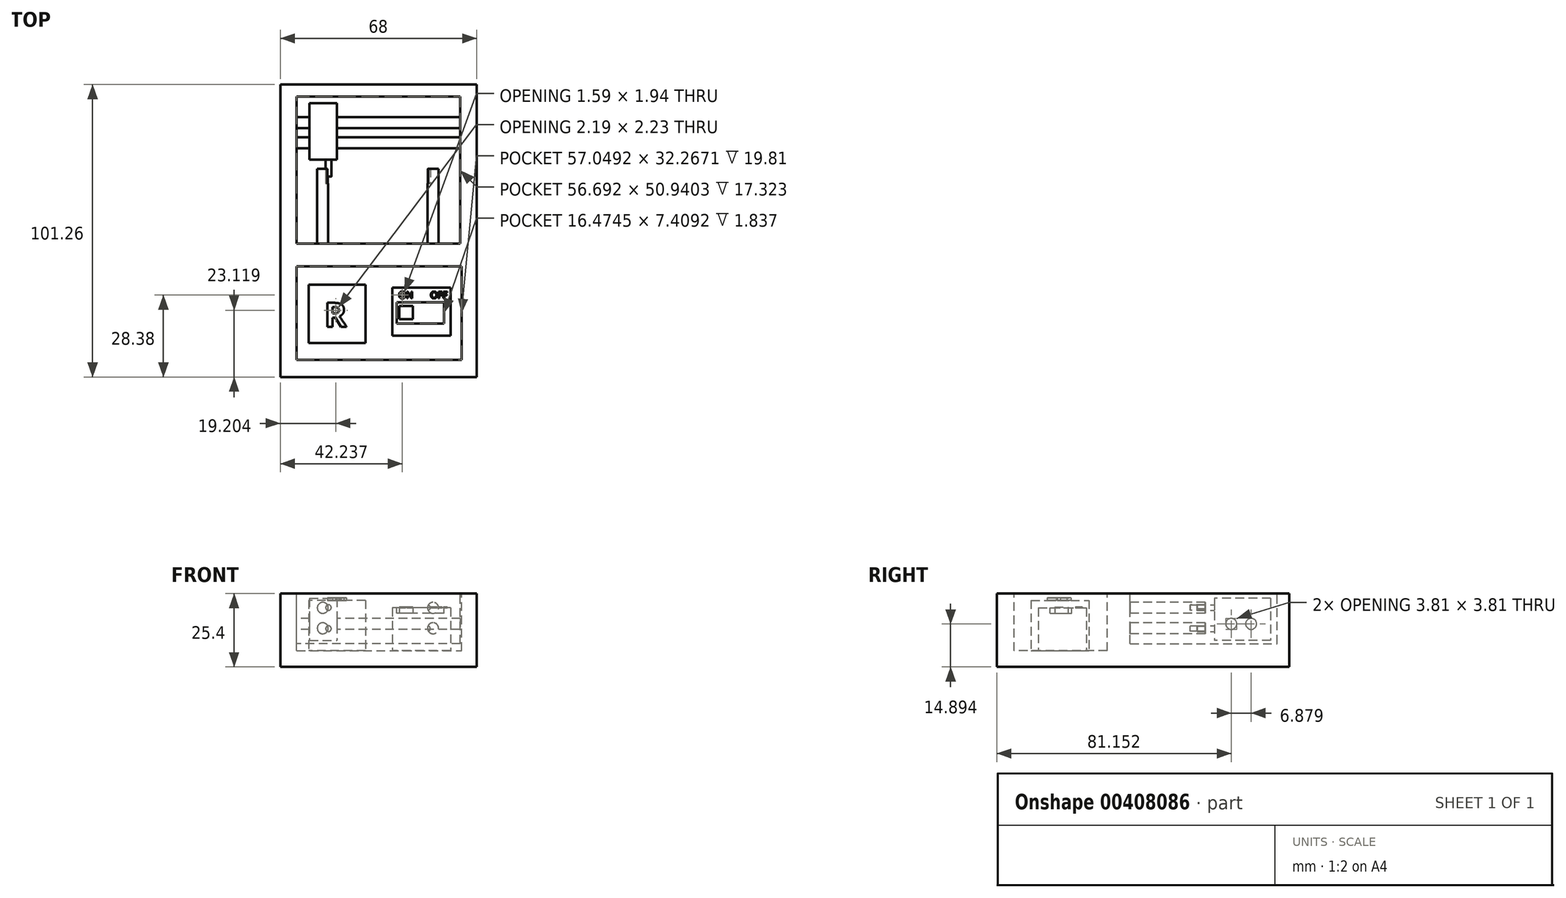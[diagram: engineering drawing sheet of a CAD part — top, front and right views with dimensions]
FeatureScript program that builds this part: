
annotation { "Feature Type Name" : "Feature", "Feature Type Description" : "" }
export const myFeature = defineFeature(function(context is Context, id is Id, definition is map)
    precondition{}
    {
        {
            var Q0;
            Q0=qCreatedBy(makeId("Top.planeOp"),FACE);
            var sketch = newSketch(context, id + "F0", { "sketchPlane" : qUnion([Q0])});
            skLineSegment(sketch, "E0.bottom", {"start": v(34, -50.63) * mm, "end": v(-34, -50.63) * mm});
            skLineSegment(sketch, "E0.top", {"start": v(34, 50.63) * mm, "end": v(-34, 50.63) * mm});
            skLineSegment(sketch, "E0.left", {"start": v(34, -50.63) * mm, "end": v(34, 50.63) * mm});
            skLineSegment(sketch, "E0.right", {"start": v(-34, -50.63) * mm, "end": v(-34, 50.63) * mm});
            skPoint(sketch, "E0.middle", {"position": v(0, 0) * mm});
            skSolve(sketch);
        }
        {
            var Q0;
            Q0 = qSketchRegion(id + "F0", true);
            extrude(context, id + "F1", {"entities" : qUnion([Q0]), "depth" : 25.4 * mm});
        }
        {
            var Q0;
            Q0=makeQuery(id+"F1.opExtrude","CAP_FACE",FACE,{"disambiguationData":[OSD([sQuery(id+"F0.wireOp",EDGE,"E0.bottom"),sQuery(id+"F0.wireOp",EDGE,"E0.top"),sQuery(id+"F0.wireOp",EDGE,"E0.left"),sQuery(id+"F0.wireOp",EDGE,"E0.right")])],"isStart":false});
            var sketch = newSketch(context, id + "F2", { "sketchPlane" : qUnion([Q0])});
            skLineSegment(sketch, "E1.bottom", {"start": v(-28.3, -12.38) * mm, "end": v(28.74, -12.38) * mm});
            skLineSegment(sketch, "E1.top", {"start": v(-28.3, -44.65) * mm, "end": v(28.74, -44.65) * mm});
            skLineSegment(sketch, "E1.left", {"start": v(-28.3, -12.38) * mm, "end": v(-28.3, -44.65) * mm});
            skLineSegment(sketch, "E1.right", {"start": v(28.74, -12.38) * mm, "end": v(28.74, -44.65) * mm});
            skSolve(sketch);
        }
        {
            var Q0;
            Q0=makeQuery(id+"F2.imprint","IMPRINT",FACE,{"disambiguationData":[TD([[makeQuery(id+"F2.imprint","IMPRINT",EDGE,{"derivedFrom":sQuery(id+"F2.wireOp",EDGE,"E1.bottom")}),-1.0]])]});
            extrude(context, id + "F3", {"entities" : qUnion([Q0]), "operationType" : NewBodyOperationType.REMOVE, "oppositeDirection" : true, "depth" : 19.8 * mm});
        }
        {
            var Q0;
            Q0=makeQuery(id+"F3.boolean.opBoolean","COPY",FACE,{"derivedFrom":makeQuery(id+"F3.opExtrude","CAP_FACE",FACE,{"disambiguationData":[OSD([sQuery(id+"F2.wireOp",EDGE,"E1.bottom"),sQuery(id+"F2.wireOp",EDGE,"E1.top"),sQuery(id+"F2.wireOp",EDGE,"E1.left"),sQuery(id+"F2.wireOp",EDGE,"E1.right")])],"isStart":false})});
            var sketch = newSketch(context, id + "F4", { "sketchPlane" : qUnion([Q0])});
            skLineSegment(sketch, "E2.bottom", {"start": v(-4.5, -38.83) * mm, "end": v(-24.11, -38.83) * mm});
            skLineSegment(sketch, "E2.top", {"start": v(-4.5, -18.71) * mm, "end": v(-24.11, -18.71) * mm});
            skLineSegment(sketch, "E2.left", {"start": v(-4.5, -38.83) * mm, "end": v(-4.5, -18.71) * mm});
            skLineSegment(sketch, "E2.right", {"start": v(-24.11, -38.83) * mm, "end": v(-24.11, -18.71) * mm});
            skPoint(sketch, "E2.middle", {"position": v(-14.3, -28.77) * mm});
            skSolve(sketch);
        }
        {
            var Q0;
            Q0 = qSketchRegion(id + "F4", true);
            extrude(context, id + "F5", {"entities" : qUnion([Q0]), "depth" : 17.46 * mm});
        }
        {
            var Q0;
            Q0=makeQuery(id+"F5.opExtrude","CAP_FACE",FACE,{"disambiguationData":[OSD([sQuery(id+"F4.wireOp",EDGE,"E2.bottom"),sQuery(id+"F4.wireOp",EDGE,"E2.top"),sQuery(id+"F4.wireOp",EDGE,"E2.left"),sQuery(id+"F4.wireOp",EDGE,"E2.right")])],"isStart":false});
            var sketch = newSketch(context, id + "F6", { "sketchPlane" : qUnion([Q0])});
            skText(sketch, "E3", { "text": "R", "fontName": "OpenSans-Bold.ttf"});
            const initialGuessF6  = {"E3": [-0.01868, -0.03322, 1, 0, 0.00833]};
            skSetInitialGuess(sketch, initialGuessF6);
            skSolve(sketch);
        }
        {
            var Q0;
            Q0 = qSketchRegion(id + "F6", true);
            extrude(context, id + "F7", {"entities" : qUnion([Q0]), "depth" : 0.9 * mm});
        }
        {
            var Q0;
            Q0=makeQuery(id+"F3.boolean.opBoolean","COPY",FACE,{"derivedFrom":makeQuery(id+"F3.opExtrude","CAP_FACE",FACE,{"disambiguationData":[OSD([sQuery(id+"F2.wireOp",EDGE,"E1.bottom"),sQuery(id+"F2.wireOp",EDGE,"E1.top"),sQuery(id+"F2.wireOp",EDGE,"E1.left"),sQuery(id+"F2.wireOp",EDGE,"E1.right")])],"isStart":false})});
            var sketch = newSketch(context, id + "F8", { "sketchPlane" : qUnion([Q0])});
            skLineSegment(sketch, "E4.bottom", {"start": v(24.93, -36.28) * mm, "end": v(4.85, -36.28) * mm});
            skLineSegment(sketch, "E4.top", {"start": v(24.93, -19.66) * mm, "end": v(4.85, -19.66) * mm});
            skLineSegment(sketch, "E4.left", {"start": v(24.93, -36.28) * mm, "end": v(24.93, -19.66) * mm});
            skLineSegment(sketch, "E4.right", {"start": v(4.85, -36.28) * mm, "end": v(4.85, -19.66) * mm});
            skPoint(sketch, "E4.middle", {"position": v(14.9, -27.97) * mm});
            skSolve(sketch);
        }
        {
            var Q0;
            Q0 = qSketchRegion(id + "F8", true);
            extrude(context, id + "F9", {"entities" : qUnion([Q0]), "depth" : 14.86 * mm});
        }
        {
            var Q0;
            Q0=makeQuery(id+"F9.opExtrude","CAP_FACE",FACE,{"disambiguationData":[OSD([sQuery(id+"F8.wireOp",EDGE,"E4.bottom"),sQuery(id+"F8.wireOp",EDGE,"E4.top"),sQuery(id+"F8.wireOp",EDGE,"E4.left"),sQuery(id+"F8.wireOp",EDGE,"E4.right")])],"isStart":false});
            var sketch = newSketch(context, id + "F10", { "sketchPlane" : qUnion([Q0])});
            skLineSegment(sketch, "E5.bottom", {"start": v(22.74, -32.16) * mm, "end": v(6.27, -32.16) * mm});
            skLineSegment(sketch, "E5.top", {"start": v(22.74, -24.75) * mm, "end": v(6.27, -24.75) * mm});
            skLineSegment(sketch, "E5.left", {"start": v(22.74, -32.16) * mm, "end": v(22.74, -24.75) * mm});
            skLineSegment(sketch, "E5.right", {"start": v(6.27, -32.16) * mm, "end": v(6.27, -24.75) * mm});
            skPoint(sketch, "E5.middle", {"position": v(14.5, -28.45) * mm});
            skSolve(sketch);
        }
        {
            var Q0;
            Q0 = qSketchRegion(id + "F10", true);
            extrude(context, id + "F11", {"entities" : qUnion([Q0]), "operationType" : NewBodyOperationType.REMOVE, "oppositeDirection" : true, "depth" : 1.84 * mm});
        }
        {
            var Q0;
            Q0=makeQuery(id+"F11.boolean.opBoolean","COPY",FACE,{"derivedFrom":makeQuery(id+"F11.opExtrude","CAP_FACE",FACE,{"disambiguationData":[OSD([sQuery(id+"F10.wireOp",EDGE,"E5.bottom"),sQuery(id+"F10.wireOp",EDGE,"E5.top"),sQuery(id+"F10.wireOp",EDGE,"E5.left"),sQuery(id+"F10.wireOp",EDGE,"E5.right")])],"isStart":false})});
            var sketch = newSketch(context, id + "F12", { "sketchPlane" : qUnion([Q0])});
            skLineSegment(sketch, "E6.bottom", {"start": v(11.86, -30.6) * mm, "end": v(7.21, -30.6) * mm});
            skLineSegment(sketch, "E6.top", {"start": v(11.86, -26) * mm, "end": v(7.21, -26) * mm});
            skLineSegment(sketch, "E6.left", {"start": v(11.86, -30.6) * mm, "end": v(11.86, -26) * mm});
            skLineSegment(sketch, "E6.right", {"start": v(7.21, -30.6) * mm, "end": v(7.21, -26) * mm});
            skPoint(sketch, "E6.middle", {"position": v(9.54, -28.3) * mm});
            skSolve(sketch);
        }
        {
            var Q0;
            Q0 = qSketchRegion(id + "F12", true);
            extrude(context, id + "F13", {"entities" : qUnion([Q0]), "depth" : 2.07 * mm});
        }
        {
            var Q0;
            Q0=makeQuery(id+"F9.opExtrude","CAP_FACE",FACE,{"disambiguationData":[OSD([sQuery(id+"F8.wireOp",EDGE,"E4.bottom"),sQuery(id+"F8.wireOp",EDGE,"E4.top"),sQuery(id+"F8.wireOp",EDGE,"E4.left"),sQuery(id+"F8.wireOp",EDGE,"E4.right")])],"isStart":false});
            var sketch = newSketch(context, id + "F14", { "sketchPlane" : qUnion([Q0])});
            skText(sketch, "E7", { "text": "ON", "fontName": "OpenSans-Regular.ttf"});
            skText(sketch, "E8", { "text": "OFF", "fontName": "OpenSans-Regular.ttf"});
            const initialGuessF14  = {"E7": [0.00695, -0.02343, 1, 0, 0.00238], "E8": [0.01795, -0.0234, 1, 0, 0.00235]};
            skSetInitialGuess(sketch, initialGuessF14);
            skSolve(sketch);
        }
        {
            var Q0;
            Q0 = qSketchRegion(id + "F14", true);
            extrude(context, id + "F15", {"entities" : qUnion([Q0]), "depth" : 0.22 * mm});
        }
        {
            var Q0;
            Q0=makeQuery(id+"F1.opExtrude","CAP_FACE",FACE,{"disambiguationData":[OSD([sQuery(id+"F0.wireOp",EDGE,"E0.bottom"),sQuery(id+"F0.wireOp",EDGE,"E0.top"),sQuery(id+"F0.wireOp",EDGE,"E0.left"),sQuery(id+"F0.wireOp",EDGE,"E0.right")])],"isStart":false});
            var sketch = newSketch(context, id + "F16", { "sketchPlane" : qUnion([Q0])});
            skLineSegment(sketch, "E9.bottom", {"start": v(28.35, -4.48) * mm, "end": v(-28.35, -4.48) * mm});
            skLineSegment(sketch, "E9.top", {"start": v(28.35, 46.46) * mm, "end": v(-28.35, 46.46) * mm});
            skLineSegment(sketch, "E9.left", {"start": v(28.35, -4.48) * mm, "end": v(28.35, 46.46) * mm});
            skLineSegment(sketch, "E9.right", {"start": v(-28.35, -4.48) * mm, "end": v(-28.35, 46.46) * mm});
            skPoint(sketch, "E9.middle", {"position": v(0, 20.99) * mm});
            skSolve(sketch);
        }
        {
            var Q0;
            Q0 = qSketchRegion(id + "F16", true);
            extrude(context, id + "F17", {"entities" : qUnion([Q0]), "operationType" : NewBodyOperationType.REMOVE, "oppositeDirection" : true, "depth" : 17.32 * mm});
        }
        {
            var Q0;
            Q0=makeQuery(id+"F17.boolean.opBoolean","COPY",FACE,{"derivedFrom":makeQuery(id+"F17.opExtrude","SWEPT_FACE",FACE,{"disambiguationData":[OSD([sQuery(id+"F16.wireOp",EDGE,"E9.bottom")])]})});
            var sketch = newSketch(context, id + "F18", { "sketchPlane" : qUnion([Q0])});
            skCircle(sketch, "E10", {"center": v(-18.89, 20.44) * mm, "radius": 1.9 * mm});
            skCircle(sketch, "E11", {"center": v(-18.89, 13.37) * mm, "radius": 1.9 * mm});
            skCircle(sketch, "E12", {"center": v(19.28, 13.37) * mm, "radius": 1.9 * mm});
            skCircle(sketch, "E13", {"center": v(19.28, 20.44) * mm, "radius": 1.9 * mm});
            skSolve(sketch);
        }
        {
            var Q0;
            Q0 = qSketchRegion(id + "F18", true);
            extrude(context, id + "F19", {"entities" : qUnion([Q0]), "operationType" : NewBodyOperationType.ADD, "depth" : 25.96 * mm});
        }
        {
            var Q0;
            Q0 = qSketchRegion(id + "F18", true);
            var sketch = newSketch(context, id + "F20", { "sketchPlane" : qUnion([Q0])});
            skCircle(sketch, "E14", {"center": v(-17, 20.5) * mm, "radius": 0.95 * mm});
            skCircle(sketch, "E15", {"center": v(-17, 13.23) * mm, "radius": 0.95 * mm});
            skCircle(sketch, "E16", {"center": v(17.31, 13.23) * mm, "radius": 0.95 * mm});
            skCircle(sketch, "E17", {"center": v(17.31, 20.5) * mm, "radius": 0.95 * mm});
            skSolve(sketch);
        }
        {
            var Q0;
            Q0 = qSketchRegion(id + "F20", true);
            extrude(context, id + "F21", {"entities" : qUnion([Q0]), "operationType" : NewBodyOperationType.REMOVE, "depth" : 46.95 * mm, "hasSecondDirection" : true, "secondDirectionOppositeDirection" : false, "secondDirectionDepth" : 20.8 * mm});
        }
        {
            var Q0;
            Q0=makeQuery(id+"F17.boolean.opBoolean","COPY",FACE,{"derivedFrom":makeQuery(id+"F17.opExtrude","SWEPT_FACE",FACE,{"disambiguationData":[OSD([sQuery(id+"F16.wireOp",EDGE,"E9.right")])]})});
            var sketch = newSketch(context, id + "F22", { "sketchPlane" : qUnion([Q0])});
            skCircle(sketch, "E18", {"center": v(30.52, 14.9) * mm, "radius": 1.9 * mm});
            skCircle(sketch, "E19", {"center": v(37.4, 14.9) * mm, "radius": 1.9 * mm});
            skSolve(sketch);
        }
        {
            var Q0;
            Q0 = qSketchRegion(id + "F22", true);
            extrude(context, id + "F23", {"entities" : qUnion([Q0]), "operationType" : NewBodyOperationType.ADD, "depth" : 58.25 * mm});
        }
        {
            var Q0;
            Q0=makeQuery(id+"F17.boolean.opBoolean","COPY",FACE,{"derivedFrom":makeQuery(id+"F17.opExtrude","SWEPT_FACE",FACE,{"disambiguationData":[OSD([sQuery(id+"F16.wireOp",EDGE,"E9.bottom")])]})});
            var sketch = newSketch(context, id + "F24", { "sketchPlane" : qUnion([Q0])});
            skLineSegment(sketch, "E20.bottom", {"start": v(23.88, 23.77) * mm, "end": v(14.44, 23.77) * mm});
            skLineSegment(sketch, "E20.top", {"start": v(23.88, 9.13) * mm, "end": v(14.44, 9.13) * mm});
            skLineSegment(sketch, "E20.left", {"start": v(23.88, 23.77) * mm, "end": v(23.88, 9.13) * mm});
            skLineSegment(sketch, "E20.right", {"start": v(14.44, 23.77) * mm, "end": v(14.44, 9.13) * mm});
            skSolve(sketch);
        }
        {
            var Q0;
            Q0 = qSketchRegion(id + "F24", true);
            extrude(context, id + "F25", {"entities" : qUnion([Q0]), "depth" : 48.63 * mm, "hasSecondDirection" : true, "secondDirectionOppositeDirection" : false, "secondDirectionDepth" : 29.17 * mm});
        }
        {
            var Q0;
            Q0=makeQuery(id+"F25.opExtrude","CAP_FACE",FACE,{"disambiguationData":[OSD([sQuery(id+"F24.wireOp",EDGE,"E20.bottom"),sQuery(id+"F24.wireOp",EDGE,"E20.top"),sQuery(id+"F24.wireOp",EDGE,"E20.left"),sQuery(id+"F24.wireOp",EDGE,"E20.right")])],"isStart":false});
            var sketch = newSketch(context, id + "F26", { "sketchPlane" : qUnion([Q0])});
            skCircle(sketch, "E21", {"center": v(17.3, 13.22) * mm, "radius": 0.98 * mm});
            skCircle(sketch, "E22", {"center": v(17.3, 20.54) * mm, "radius": 0.97 * mm});
            skSolve(sketch);
        }
        {
            var Q0;
            Q0 = qSketchRegion(id + "F26", true);
            extrude(context, id + "F27", {"entities" : qUnion([Q0]), "operationType" : NewBodyOperationType.ADD, "oppositeDirection" : true, "depth" : 25.4 * mm});
        }
    });
